# Revit family: PRD_FrankeWS_WasteBins_EXOSWasteBin_EXOS605X,605B,605W
name_source: partatom
category: Furniture
revit_build: Autodesk Revit 2018 (Build: 20190510_1515(x64)
units: mm (PartAtom-declared; Revit-internal decimal feet)

## family parameters
Cut with Voids When Loaded = No
Host = Face
OmniClass Number = 23.40.20.31.11
OmniClass Title = Bins
Room Calculation Point = No
Shared = No

## types (3) — shared parameters
AssetType = Fixed
BagHolder = Integrated
Category = Pr_40_50_07_96, Waste bins
Color = Stainless steel
Default Elevation = 820 mm  [stored 2.69029 ft]
DurationUnit = year
Features = stainless steel, 1.20 mm, satin finished, for wall mounting
FillingVolume = 30.00 liter
Finish = Satin finished
FinishAndColour = Stainless steel, satin finished
Form = Wall mounted
IfcExportAs = IfcFurnitureType
IfcExportType = NOTDEFINED
IntegralAccessories = Includes mounting materials
Lid = no
Lock = key-lock
MainColor = Stainless steel
Manufacturer = KWC Group AG
ManufacturerName = KWC Group AG
ManufacturerURL = www.kwc.com
Material = Stainless steel
Materials = Stainless steel 1.4301
NBSDescription = Waste bins
NBSReference = 45-35-72/380
NominalDepth = 250 mm  [stored 0.82021 ft]
NominalHeight = 573 mm  [stored 1.87992 ft]
NominalWidth = 300 mm  [stored 0.984252 ft]
ProductInformation = https://pim.kwc.com
Size = 300 x 573 x 250 mm
Style = Waste bin
SurfaceTreatment = InoxPlus (anti fingerprint)
URL = www.kwc.com
Uniclass2015Code = Pr_40_50_07_96
Uniclass2015Title = Waste bins
Uniclass2015Version = Products v1.10
Version = 1
WarrantyDurationUnit = year
WasteBinMaterial = PRD_AR_StainlessSteel_SatinFinished

## per-type parameters (varying)
| type | BIMObjectName | Description | GrossWeight | ModelNumber | Name | NetWeight | WasteBinFrontMaterial |
| EXOS605B | PRD_AR_WasteBins_EXOS_WasteBin_EXOS605B | Waste bin for wall mounting, stainless steel with satin finish, black safety glass front panel, casing with InoxPlus surface refinement for the reduction of finger marks and better cleaning characteristics (easy to clean), material thickness 1.2 mm, capacity approximate 30 litres, integrated bag holder, includes mounting bracket and mounting materials. | 11.67 kg | 2030022929 | EXOS Waste bin EXOS605B | 10.60 kg | PRD_AR_Glass_Black |
| EXOS605X | PRD_AR_WasteBins_EXOS_WasteBin_EXOS605X | Waste bin for wall mounting, stainless steel with satin finish, front and casing with InoxPlus surface refinement for the reduction of finger marks and better cleaning characteristics (easy to clean), material thickness 1.2 mm, capacity approximate 30 litres, integrated bag holder, includes mounting bracket and mounting materials. | 10.31 kg | 2030022928 | EXOS Waste bin EXOS605X | 9.22 kg | PRD_AR_StainlessSteel_SatinFinished |
| EXOS605W | PRD_AR_WasteBins_EXOS_WasteBin_EXOS605W | Waste bin for wall mounting, stainless steel with satin finish, white safety glass front panel, casing with InoxPlus surface refinement for the reduction of finger marks and better cleaning characteristics (easy to clean), material thickness 1.2 mm, capacity approximate 30 litres, integrated bag holder, includes mounting bracket and mounting materials. | 11.80 kg | 2030025228 | EXOS Waste bin EXOS605W | 10.10 kg | PRD_AR_Glass_White |

note: column(s) folded — value = type name in every type: Model, ModelReference

note: [stored X ft] marks values corroborated as IEEE doubles in the binary element streams (Revit-internal decimal feet)

## geometry (parser evidence)
native form markers: Sweep x2
no freeform markers — native parametric forms only
